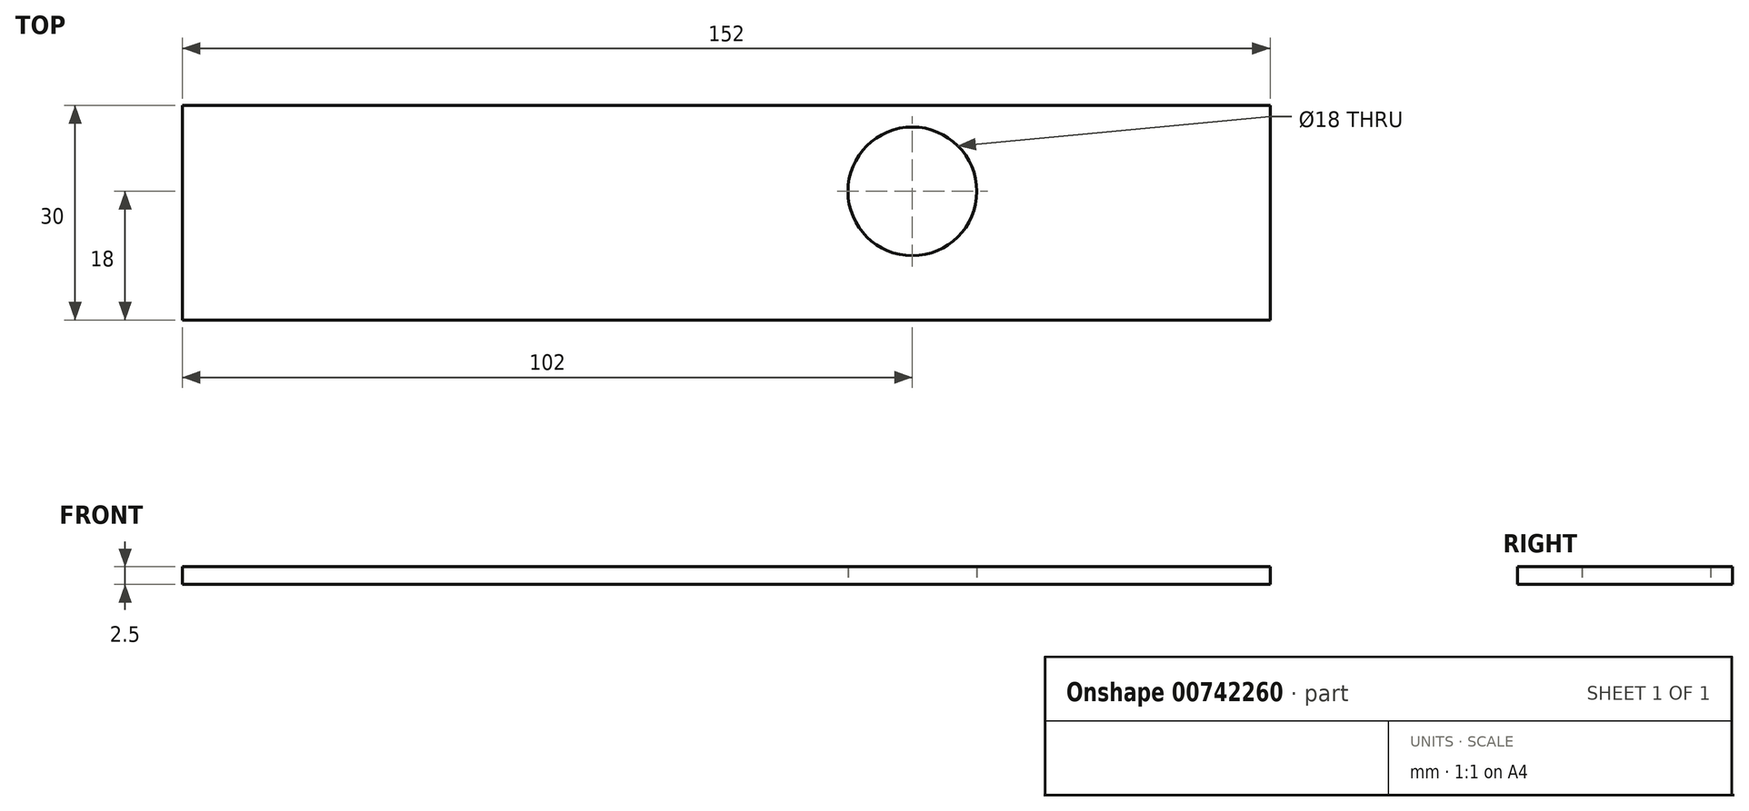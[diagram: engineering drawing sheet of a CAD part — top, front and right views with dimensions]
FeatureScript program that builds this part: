
annotation { "Feature Type Name" : "Feature", "Feature Type Description" : "" }
export const myFeature = defineFeature(function(context is Context, id is Id, definition is map)
    precondition{}
    {
        {
            var Q0;
            Q0=qCreatedBy(makeId("Top.planeOp"),FACE);
            var sketch = newSketch(context, id + "F0", { "sketchPlane" : qUnion([Q0])});
            skCircle(sketch, "E0", {"center": v(0, 0) * mm, "radius": 9 * mm});
            skLineSegment(sketch, "E1.bottom", {"start": v(-102, 12) * mm, "end": v(50, 12) * mm});
            skLineSegment(sketch, "E1.top", {"start": v(-102, -18) * mm, "end": v(50, -18) * mm});
            skLineSegment(sketch, "E1.left", {"start": v(-102, 12) * mm, "end": v(-102, -18) * mm});
            skLineSegment(sketch, "E1.right", {"start": v(50, 12) * mm, "end": v(50, -18) * mm});
            skSolve(sketch);
        }
        {
            var Q0;
            Q0=makeQuery(id+"F0.imprint","IMPRINT",FACE,{"disambiguationData":[TD([[makeQuery(id+"F0.imprint","IMPRINT",EDGE,{"derivedFrom":sQuery(id+"F0.wireOp",EDGE,"E0")}),-1.0]])]});
            extrude(context, id + "F1", {"entities" : qUnion([Q0]), "depth" : 2.5 * mm, "offsetDistance" : 25 * mm});
        }
    });
